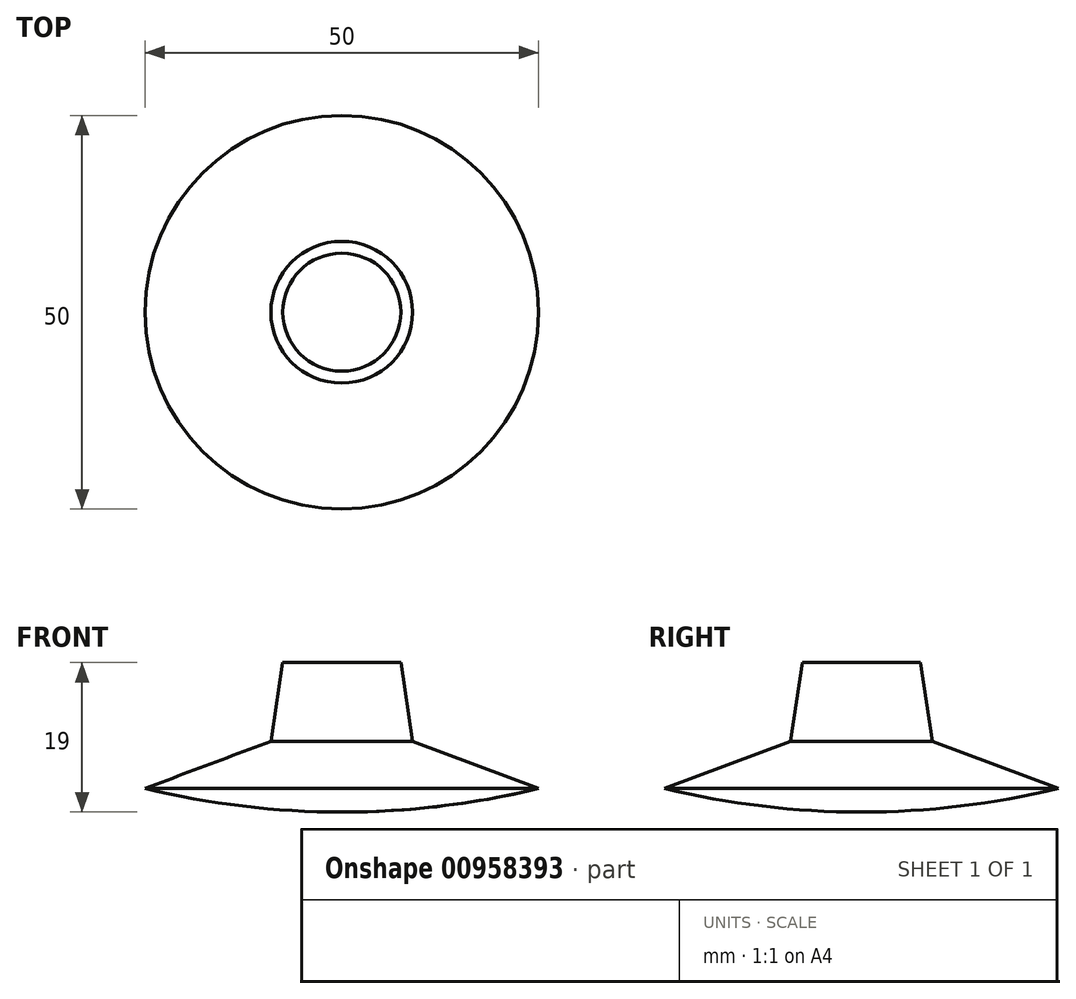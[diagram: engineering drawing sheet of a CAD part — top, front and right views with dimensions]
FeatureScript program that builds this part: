
annotation { "Feature Type Name" : "Feature", "Feature Type Description" : "" }
export const myFeature = defineFeature(function(context is Context, id is Id, definition is map)
    precondition{}
    {
        {
            var Q0;
            Q0=qCreatedBy(makeId("Front.planeOp"),FACE);
            var sketch = newSketch(context, id + "F0", { "sketchPlane" : qUnion([Q0])});
            skLineSegment(sketch, "E0", {"start": v(0, 0) * mm, "end": v(0, 19) * mm});
            skLineSegment(sketch, "E1", {"start": v(0, 19) * mm, "end": v(7.5, 19) * mm});
            skLineSegment(sketch, "E2", {"start": v(7.5, 19) * mm, "end": v(9, 9) * mm});
            skLineSegment(sketch, "E3", {"start": v(9, 9) * mm, "end": v(25, 3) * mm});
            skArc(sketch, "E4", {"start": v(0, 0) * mm, "mid": v(12.59, 0.75) * mm, "end": v(25, 3) * mm});
            skLineSegment(sketch, "E5", {"start": v(1.67, 0) * mm, "end": v(29.67, 0) * mm, "construction": true});
            skSolve(sketch);
        }
        {
            var Q0;
            Q0=makeQuery(id+"F0.imprint","IMPRINT",FACE,{"disambiguationData":[TD([[makeQuery(id+"F0.imprint","IMPRINT",EDGE,{"derivedFrom":sQuery(id+"F0.wireOp",EDGE,"E0")}),-1.0]])]});
            var Q1;
            Q1=sQuery(id+"F0.wireOp",EDGE,"E0");
            revolve(context, id + "F1", {"surfaceOperationType" : NewSurfaceOperationType.NEW, "entities" : qUnion([Q0]), "axis" : qUnion([Q1]), "revolveType" : RevolveType.FULL});
        }
    });
